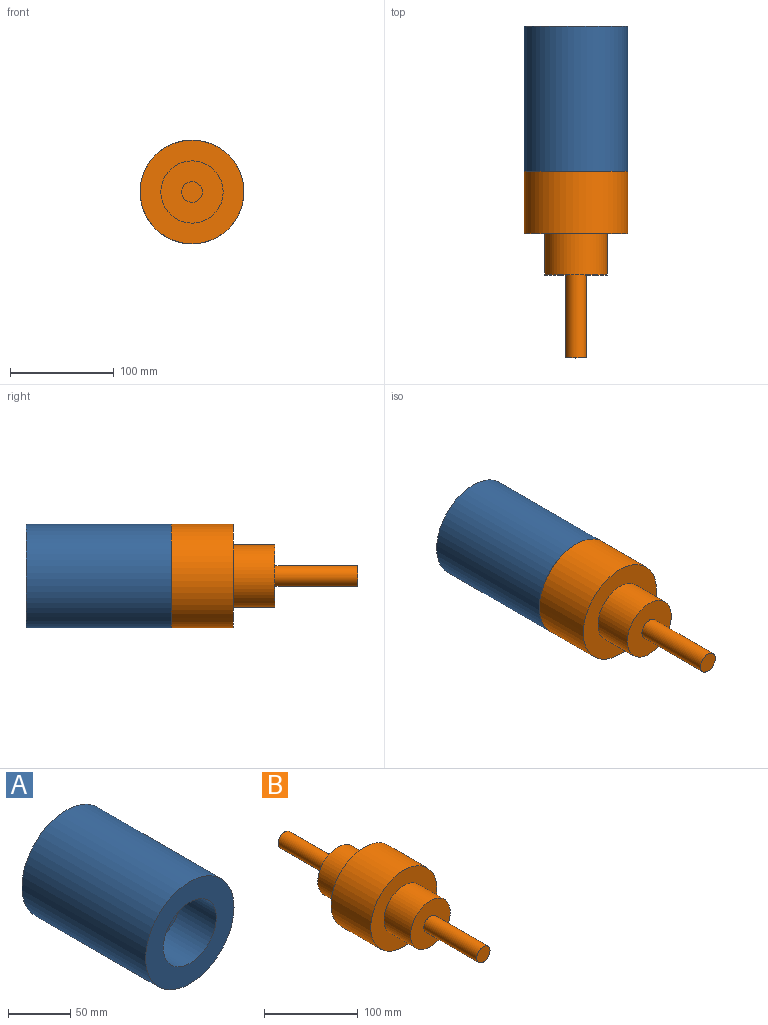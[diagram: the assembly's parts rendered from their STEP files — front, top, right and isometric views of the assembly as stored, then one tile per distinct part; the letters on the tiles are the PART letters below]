
ASSEMBLY  parts=2 mates=1
PART A: 7 faces, bbox 100x140x100 mm
  f0: cylinder r=50mm len=140mm, axis (0,1,0), area 43982.3mm2, adj f1,f2
  f1: plane 100x100mm, normal (0,-1,0), area 5026.5mm2, adj f0,f3
  f2: plane 100x100mm, normal (0,1,0), area 7854mm2, adj f0
  f3: cylinder r=30mm len=60mm, axis (0,-1,0), area 7539.8mm2, adj f1,f4
  f4: plane 60x60mm, normal (0,-1,0), area 2513.3mm2, adj f3,f5
  f5: cylinder r=10mm len=80mm, axis (0,-1,0), area 5026.5mm2, adj f4,f6
  f6: plane 20x20mm, normal (0,-1,0), area 314.2mm2, adj f5
PART B: 11 faces, bbox 100x300x100 mm
  f0: cylinder r=50mm len=100mm, axis (0,1,0), area 18849.6mm2, adj f1,f2
  f1: plane 100x100mm, normal (0,-1,0), area 5026.5mm2, adj f0,f3
  f2: plane 100x100mm, normal (0,1,0), area 5026.5mm2, adj f0,f7
  f3: cylinder r=30mm len=60mm, axis (0,1,0), area 7539.8mm2, adj f1,f4
  f4: plane 60x60mm, normal (0,-1,0), area 2513.3mm2, adj f3,f5
  f5: cylinder r=10mm len=80mm, axis (0,1,0), area 5026.5mm2, adj f4,f6
  f6: plane 20x20mm, normal (0,-1,0), area 314.2mm2, adj f5
  f7: cylinder r=30mm len=60mm, axis (0,-1,0), area 7539.8mm2, adj f2,f8
  f8: plane 60x60mm, normal (0,1,0), area 2513.3mm2, adj f7,f9
  f9: cylinder r=10mm len=80mm, axis (0,-1,0), area 5026.5mm2, adj f8,f10
  f10: plane 20x20mm, normal (0,1,0), area 314.2mm2, adj f9
PLACE A rot(axis=(0.65,0.64,0.4),0deg) t=(-122.73,111.5,-11.47)mm
PLACE B rot(axis=(0.65,0.64,0.4),0deg) t=(-122.73,-28.5,-11.47)mm
MATE fastened B.f3 <-> A.f0  axis (0,-1,0) through (-122.73,-8.5,-11.47)mm
